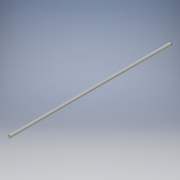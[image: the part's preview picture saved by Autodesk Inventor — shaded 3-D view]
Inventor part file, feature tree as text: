
AUTODESK INVENTOR PART (.ipt)
format: ipt  version: 2016 (Build 200138000, 138)  size: 86,528 bytes
history: native  units: in
note: dims shown in document units (in); Inventor stores cm internally (conversion verified against a paired STEP export)
features: extrude x1, sketch x1
ambient origin geometry x8: Origin, YZ Plane, XZ Plane, XY Plane, X Axis, Y Axis, Z Axis, Center Point
bodies: Solid1 (feature_tree)
feature tree (2):
  extrude  "Extrusion1"  Depth=12.0in TaperAngle=0.0deg
  sketch  "Sketch1"  dims[d0=0.188in d1=12.0in d2=0.0in]
